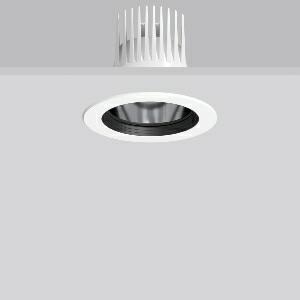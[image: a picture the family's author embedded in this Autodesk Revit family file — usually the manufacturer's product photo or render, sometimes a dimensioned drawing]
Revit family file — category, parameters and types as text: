
# Revit family: heledon_maxi_e_901758_002_3_4c09
name_source: partatom
category: Lighting Fixtures
units: mm (PartAtom-declared; Revit-internal decimal feet)

## family parameters
Cut with Voids When Loaded = No
Host = Face
Light Source = No
Part Type = Normal
Room Calculation Point = No
Round Connector Dimension = Use Diameter
Shared = No

## types (1)
- HELEDON maxi E (1 x LED Modul 935, 3400 lm, 3500)
    Apparent Load = 25 VA
    Approval mark = CE
    CIE Flux Codes = 100 100 100 100 100
    Color Rendering = 92
    Color Temperature = 3500
    Default Elevation = 1800 mm
    Description = Series: HELEDON maxi
Round recessed downlight. Housing: die-cast aluminium, powder-coated. Black plastic ring and recessed LED to prevent glare from the side. Optical assembly with reflector made of MIRO-Silver with 98% total light reflection for outstanding efficiency - can be changed without tools. Best colour rendering index Ra>90. Suitable for Recessed ceiling mounting. Installation without tools thanks to spring fastening system. Including separate LED converter with connecting cable 600 mm.High quality converter without flickering and stroboscopic effect. Through-wiring box (5 pole) available as accessory. The following accessories can be mounted without use of tools: interchangeable lenses, decorative glasses, honeycomb louvre, clear and frosted diffusers, white interchangeable plastic ring. 
Colour: traffic white, matt (RAL 9016)
Diameter: 162 mm
Height: 3 mm
Cut-out diameter: 152 mm
Recess height: 200 mm
Luminaire: recess height: 135 mm
Lamp: LED
Socket: without socket
Colour temperature: 3500K
Colour rendering index (CRI): 92
System power: 25 W
Rated luminous flux: 3400 lm
Luminous efficiency: 136 lm/W
Control gear: Regulated power supply
Protection class: II
Type of protection: IP 20
    Height = 0 mm  [stored 0 ft]
    Lamp = 1 x LED Modul 935
    Lamp Light Flux = 3400 lm
    Lamp count = 1
    Length = 162 mm
    Lifetime = 50000 h
    Luminous efficacy = 136 lm/W
    Manufacturer = RZB
    ModVariant = No
    Model = 901758.002.3
    Mounting Place = Ceiling
    Mounting Type = Recessed
    Number of Poles = 1
    OnlyDefault = Yes
    Power Factor = 1
    Product Name = HELEDON maxi E
    Product group = Recessed downlights
    ProductGroupID = 402
    Protection Class = Protection class II
    Protection Degree = IP 20
    RLX_Detail_Level = 1
    RLX_Emergency_Light_Flux = 0 lm
    RLX_Emergency_Type = 0
    RLX_Emergency_Type_DB = No
    RlxData = <blob elided: 119501 chars, md5=90eef78f>
    Socket = socket
    Standby Power = 0 W
    System Light Flux = 3400 lm
    System Power = 25 W
    Type Comments = Product without accessories
    Type Image = 901662.002.jpg
    URL = http://relux.com
    VarID = ---
    Voltage = 230 V
    Voltage Range = 220-240 V
    Weight = 0.00 kg
    Width = 0 mm  [stored 0 ft]

note: [stored X ft] marks values corroborated as IEEE doubles in the binary element streams (Revit-internal decimal feet)

## geometry (parser evidence)
native form markers: Blend x4, Sweep x11
no freeform markers — native parametric forms only
